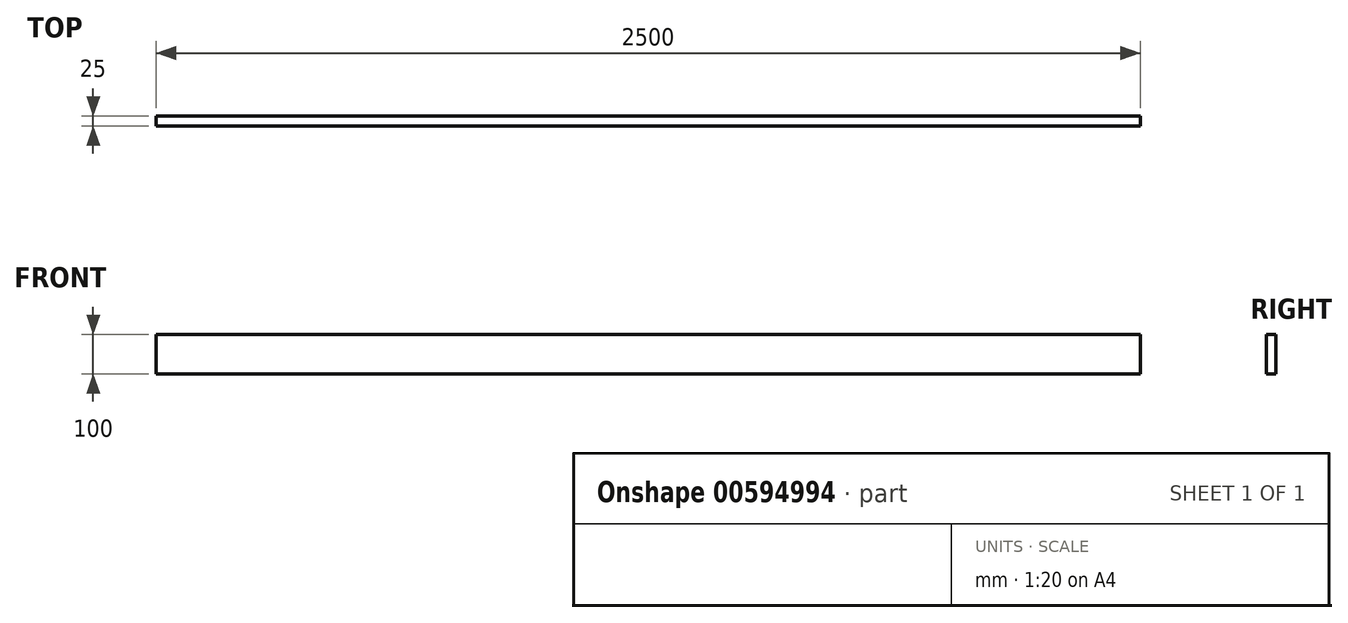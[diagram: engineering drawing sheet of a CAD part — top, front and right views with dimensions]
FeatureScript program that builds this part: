
annotation { "Feature Type Name" : "Feature", "Feature Type Description" : "" }
export const myFeature = defineFeature(function(context is Context, id is Id, definition is map)
    precondition{}
    {
        {
            var Q0;
            Q0=qCreatedBy(makeId("Front.planeOp"),FACE);
            var sketch = newSketch(context, id + "F0", { "sketchPlane" : qUnion([Q0])});
            skLineSegment(sketch, "E0.bottom", {"start": v(0, 0) * mm, "end": v(2500, 0) * mm});
            skLineSegment(sketch, "E0.top", {"start": v(0, -100) * mm, "end": v(2500, -100) * mm});
            skLineSegment(sketch, "E0.left", {"start": v(0, 0) * mm, "end": v(0, -100) * mm});
            skLineSegment(sketch, "E0.right", {"start": v(2500, 0) * mm, "end": v(2500, -100) * mm});
            skSolve(sketch);
        }
        {
            var Q0;
            Q0=makeQuery(id+"F0.imprint","IMPRINT",FACE,{"disambiguationData":[TD([[makeQuery(id+"F0.imprint","IMPRINT",EDGE,{"derivedFrom":sQuery(id+"F0.wireOp",EDGE,"E0.bottom")}),-1.0]])]});
            extrude(context, id + "F1", {"entities" : qUnion([Q0]), "depth" : 25 * mm, "offsetDistance" : 25 * mm});
        }
    });
